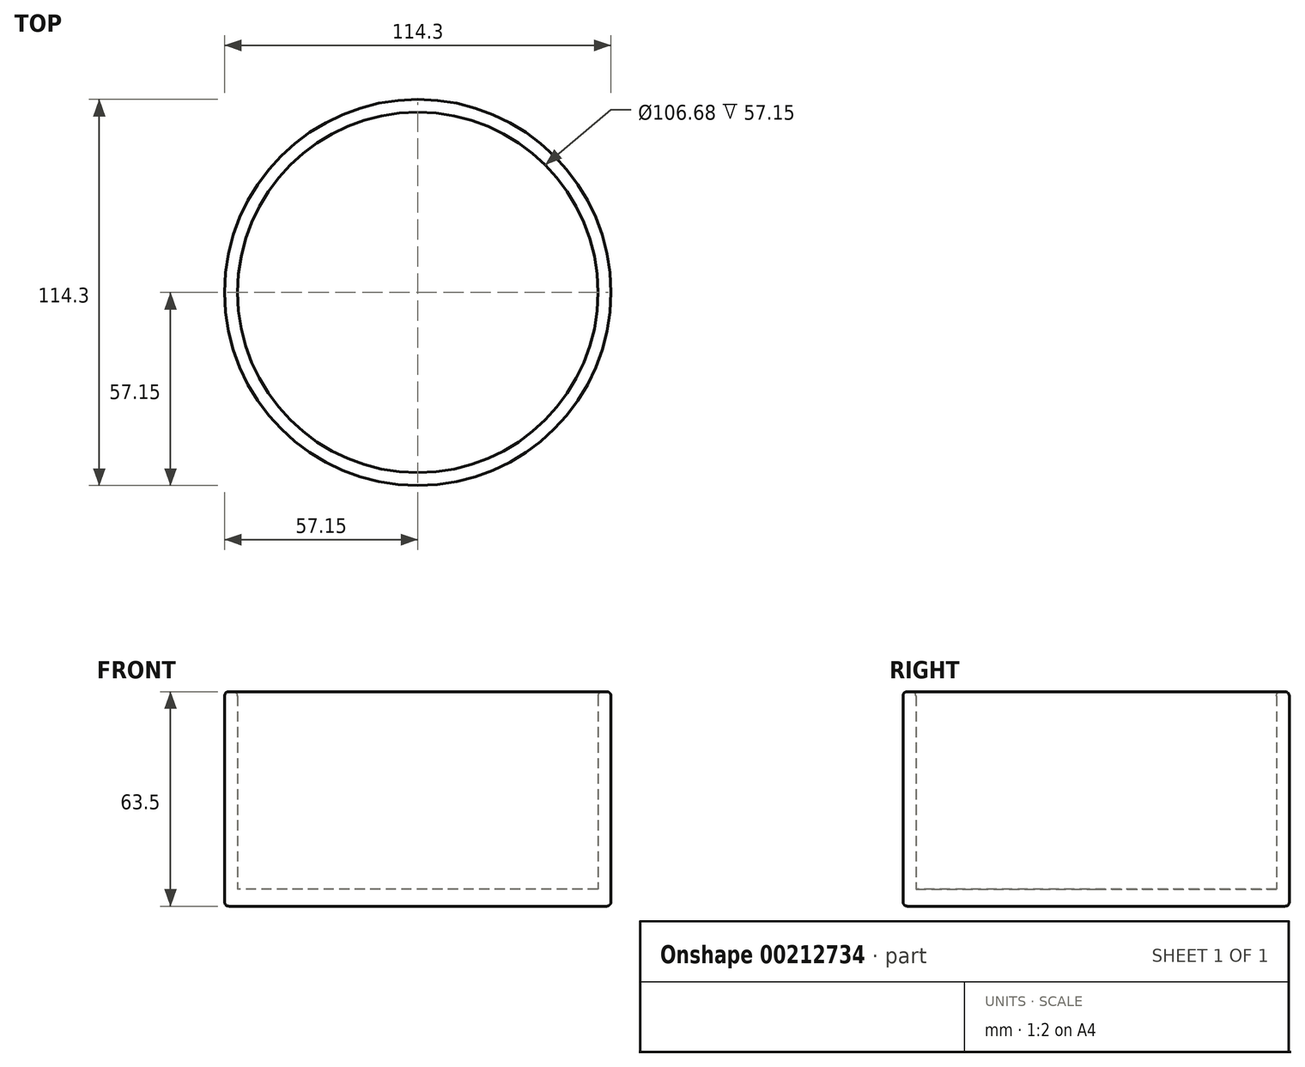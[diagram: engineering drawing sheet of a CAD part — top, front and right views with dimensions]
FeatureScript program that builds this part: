
annotation { "Feature Type Name" : "Feature", "Feature Type Description" : "" }
export const myFeature = defineFeature(function(context is Context, id is Id, definition is map)
    precondition{}
    {
        {
            var Q0;
            Q0=qCreatedBy(makeId("Top.planeOp"),FACE);
            var sketch = newSketch(context, id + "F0", { "sketchPlane" : qUnion([Q0])});
            skCircle(sketch, "E0", {"center": v(0, 0) * mm, "radius": 57.15 * mm});
            skSolve(sketch);
        }
        {
            var Q0;
            Q0=makeQuery(id+"F0.imprint","IMPRINT",FACE,{"disambiguationData":[TD([[makeQuery(id+"F0.imprint","IMPRINT",EDGE,{"derivedFrom":sQuery(id+"F0.wireOp",EDGE,"E0")}),1.0]])]});
            extrude(context, id + "F1", {"entities" : qUnion([Q0]), "depth" : 5.08 * mm});
        }
        {
            var Q0;
            Q0=makeQuery(id+"F1.opExtrude","CAP_EDGE",EDGE,{"disambiguationData":[OSD([sQuery(id+"F0.wireOp",EDGE,"E0")])],"isStart":true});
            fillet(context, id + "F2", {"entities" : qUnion([Q0]), "radius" : 1.27 * mm, "tangentPropagation" : true, "allowEdgeOverflow" : false});
        }
        {
            var Q0;
            Q0=qCreatedBy(makeId("Right.planeOp"),FACE);
            cPlane(context, id + "F3", {"entities" : qUnion([Q0]), "cplaneType" : CPlaneType.OFFSET, "offset" : 57.15 * mm, "width" : 152.4 * mm, "height" : 152.4 * mm});
        }
        {
            var Q0;
            Q0=qCreatedBy(id+"F3.planeOp",FACE);
            var sketch = newSketch(context, id + "F4", { "sketchPlane" : qUnion([Q0])});
            skLineSegment(sketch, "E1", {"start": v(0, 0) * mm, "end": v(0, 63.5) * mm});
            skSolve(sketch);
        }
        {
            var Q0;
            Q0=sQuery(id+"F4.wireOp",EDGE,"E1");
            extrude(context, id + "F5", {"bodyType" : ToolBodyType.SURFACE, "surfaceEntities" : qUnion([Q0]), "oppositeDirection" : true, "depth" : 3.8 * mm});
        }
        {
            var Q0;
            Q0=makeQuery(id+"F5.opExtrude","SWEPT_FACE",FACE,{"disambiguationData":[OSD([sQuery(id+"F4.wireOp",EDGE,"E1")])]});
            var Q1;
            Q1=makeQuery(id+"F1.opExtrude","CAP_EDGE",EDGE,{"disambiguationData":[OSD([sQuery(id+"F0.wireOp",EDGE,"E0")])],"isStart":false});
            revolve(context, id + "F6", {"operationType" : NewBodyOperationType.ADD, "entities" : qUnion([Q0]), "axis" : qUnion([Q1]), "revolveType" : RevolveType.FULL});
        }
        {
            var Q0;
            {var subQ0=sQuery(id+"F4.wireOp",VERTEX,"E1.start");Q0=makeQuery(id+"F6.opRevolve","SWEPT_EDGE",EDGE,{"disambiguationData":[OSD([subQ0]),TDD([makeQuery(id+"F5.opExtrude","CAP_VERTEX",VERTEX,{"disambiguationData":[OSD([subQ0])],"isStart":true})])]});}
            fillet(context, id + "F7", {"entities" : qUnion([Q0]), "radius" : 1.27 * mm, "tangentPropagation" : true, "allowEdgeOverflow" : false});
        }
        {
            var Q0;
            {var subQ0=sQuery(id+"F4.wireOp",VERTEX,"E1.end");Q0=makeQuery(id+"F6.opRevolve","SWEPT_EDGE",EDGE,{"disambiguationData":[OSD([subQ0]),TDD([makeQuery(id+"F5.opExtrude","CAP_VERTEX",VERTEX,{"disambiguationData":[OSD([subQ0])],"isStart":false})])]});}
            var Q1;
            {var subQ0=sQuery(id+"F4.wireOp",VERTEX,"E1.end");Q1=makeQuery(id+"F6.opRevolve","SWEPT_EDGE",EDGE,{"disambiguationData":[OSD([subQ0]),TDD([makeQuery(id+"F5.opExtrude","CAP_VERTEX",VERTEX,{"disambiguationData":[OSD([subQ0])],"isStart":true})])]});}
            fillet(context, id + "F8", {"entities" : qUnion([Q0, Q1]), "radius" : 1.27 * mm, "tangentPropagation" : true, "allowEdgeOverflow" : false});
        }
    });
